# Revit family: 8316ac
name_source: partatom
category: Plumbing Fixtures
revit_build: Autodesk Revit Architecture 2012 (Build: 20110309_2315(x64)
units: mm (PartAtom-declared; Revit-internal decimal feet)

## types (1)
- 8316ac
    ADA Compliant = Yes
    Assembly Code = D2010200
    CWFU = 2
    Cold Water Connection Diameter = 1"
    Default Elevation = 1' - 6"
    Description = 3/4 “ Battery Powered Exposed Style Urinal Flush Valve
    Documentation Link = http://www.moen.com
    Domestic Water Flow Rate = 3 GPM
    Finish = Moen-Chrome
    Flush Rate = 1.0 GPF
    HW Connection = No
    HWFU = 0
    Height = 1' - 4"
    Keynote = 15410
    Length = 0' - 6"
    Manufacturer = Moen
    Model = 8316ac
    Power Source = Battery (4xAA)
    Sensor Type = Infrared
    URL = www.moencommercial.com
    Valve Type = 3/4” IPS angle stop (vandal resistant)
    Vent Connection = No
    WFU = 0
    Waste Connection = No
    Width = 0' - 9"

## geometry (parser evidence)
native form markers: Blend x2, Sweep x7
no freeform markers — native parametric forms only
